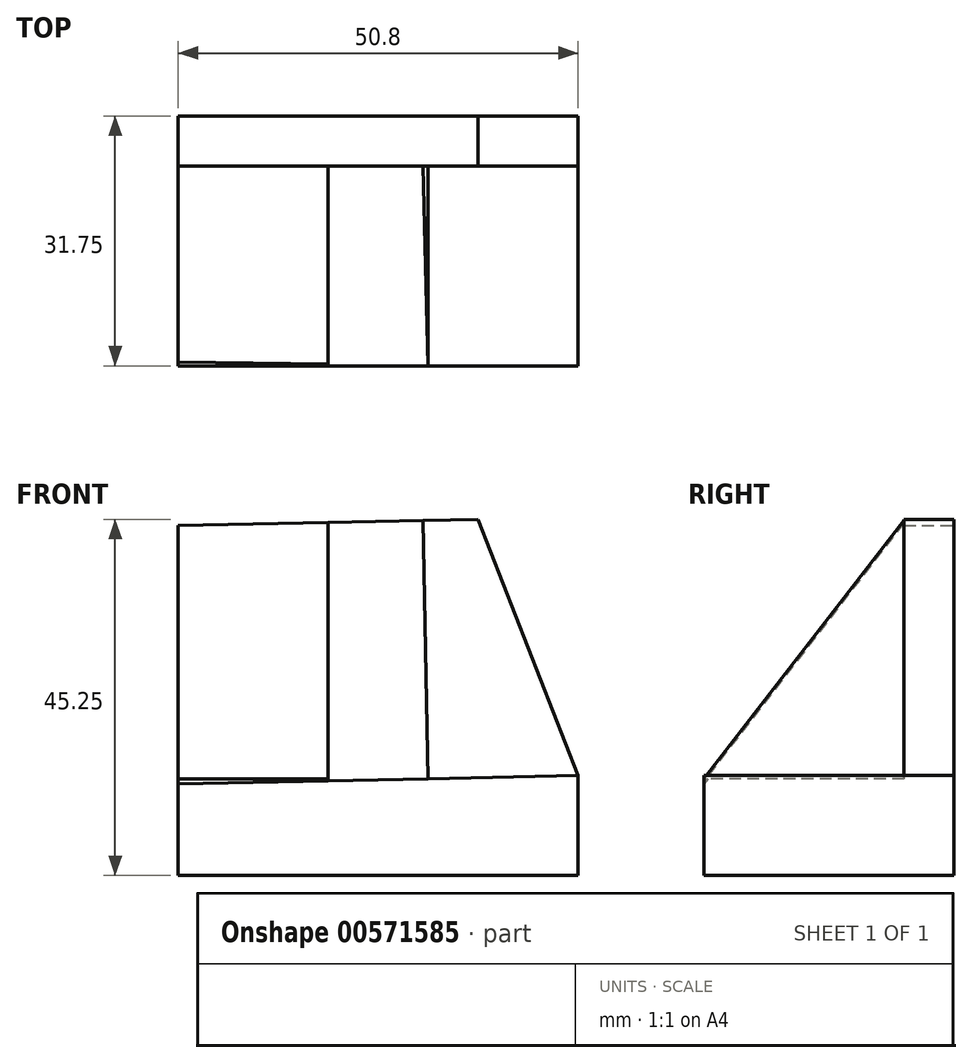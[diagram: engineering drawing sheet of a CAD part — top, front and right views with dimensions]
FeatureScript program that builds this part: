
annotation { "Feature Type Name" : "Feature", "Feature Type Description" : "" }
export const myFeature = defineFeature(function(context is Context, id is Id, definition is map)
    precondition{}
    {
        {
            var Q0;
            Q0=qCreatedBy(makeId("Front.planeOp"),FACE);
            var sketch = newSketch(context, id + "F0", { "sketchPlane" : qUnion([Q0])});
            skLineSegment(sketch, "E0", {"start": v(-57.48, 47.75) * mm, "end": v(-57.48, 3.3) * mm});
            skLineSegment(sketch, "E1", {"start": v(-57.48, 3.3) * mm, "end": v(-6.68, 3.3) * mm});
            skLineSegment(sketch, "E2", {"start": v(-6.68, 3.3) * mm, "end": v(-6.68, 16) * mm});
            skLineSegment(sketch, "E3", {"start": v(-6.68, 16) * mm, "end": v(-19.39, 48.55) * mm});
            skLineSegment(sketch, "E4", {"start": v(-19.39, 48.55) * mm, "end": v(-57.48, 47.75) * mm});
            skSolve(sketch);
        }
        {
            var Q0;
            Q0=makeQuery(id+"F0.imprint","IMPRINT",FACE,{"disambiguationData":[TD([[makeQuery(id+"F0.imprint","IMPRINT",EDGE,{"derivedFrom":sQuery(id+"F0.wireOp",EDGE,"E0")}),1.0]])]});
            extrude(context, id + "F1", {"entities" : qUnion([Q0]), "depth" : 31.75 * mm, "offsetDistance" : 25.4 * mm});
        }
        {
            var Q0;
            Q0=makeQuery(id+"F1.opExtrude","CAP_FACE",FACE,{"disambiguationData":[OSD([sQuery(id+"F0.wireOp",EDGE,"E0"),sQuery(id+"F0.wireOp",EDGE,"E1"),sQuery(id+"F0.wireOp",EDGE,"E2"),sQuery(id+"F0.wireOp",EDGE,"E3"),sQuery(id+"F0.wireOp",EDGE,"E4")])],"isStart":false});
            var sketch = newSketch(context, id + "F2", { "sketchPlane" : qUnion([Q0])});
            skLineSegment(sketch, "E5", {"start": v(-6.68, 16) * mm, "end": v(-25.72, 15.6) * mm});
            skLineSegment(sketch, "E6", {"start": v(-25.72, 15.6) * mm, "end": v(-26.41, 48.4) * mm});
            skLineSegment(sketch, "E7", {"start": v(-57.48, 15.6) * mm, "end": v(-38.43, 15.6) * mm});
            skLineSegment(sketch, "E8", {"start": v(-38.43, 15.6) * mm, "end": v(-38.43, 48.15) * mm});
            skSolve(sketch);
        }
        {
            var Q0;
            {var subQ0=sQuery(id+"F2.wireOp",EDGE,"E7");Q0=makeQuery(id+"F2.imprint","IMPRINT",FACE,{"disambiguationData":[TD([[makeQuery(id+"F2.imprint","IMPRINT",EDGE,{"derivedFrom":subQ0}),1.0]])]});}
            var Q1;
            Q1=makeQuery(id+"F2.imprint","IMPRINT",FACE,{"disambiguationData":[TD([[makeQuery(id+"F2.imprint","IMPRINT",EDGE,{"derivedFrom":sQuery(id+"F2.wireOp",EDGE,"E5")}),-1.0]])]});
            extrude(context, id + "F3", {"entities" : qUnion([Q0, Q1]), "operationType" : NewBodyOperationType.REMOVE, "oppositeDirection" : true, "depth" : 25.4 * mm, "offsetDistance" : 25.4 * mm});
        }
        {
            var Q0;
            Q0=makeQuery(id+"F3.boolean.opBoolean","COPY",FACE,{"derivedFrom":makeQuery(id+"F3.opExtrude","SWEPT_FACE",FACE,{"disambiguationData":[OSD([sQuery(id+"F2.wireOp",EDGE,"E6")])]})});
            var sketch = newSketch(context, id + "F4", { "sketchPlane" : qUnion([Q0])});
            skLineSegment(sketch, "E9", {"start": v(-6.35, 48.94) * mm, "end": v(-31.75, 16.13) * mm});
            skSolve(sketch);
        }
        {
            var Q0;
            Q0=makeQuery(id+"F4.imprint","IMPRINT",FACE,{"disambiguationData":[TD([[makeQuery(id+"F4.imprint","IMPRINT",EDGE,{"derivedFrom":sQuery(id+"F4.wireOp",EDGE,"E9")}),-1.0]])]});
            extrude(context, id + "F5", {"entities" : qUnion([Q0]), "operationType" : NewBodyOperationType.REMOVE, "endBound" : BoundingType.THROUGH_ALL, "oppositeDirection" : true, "depth" : 25.4 * mm, "offsetDistance" : 25.4 * mm});
        }
    });
